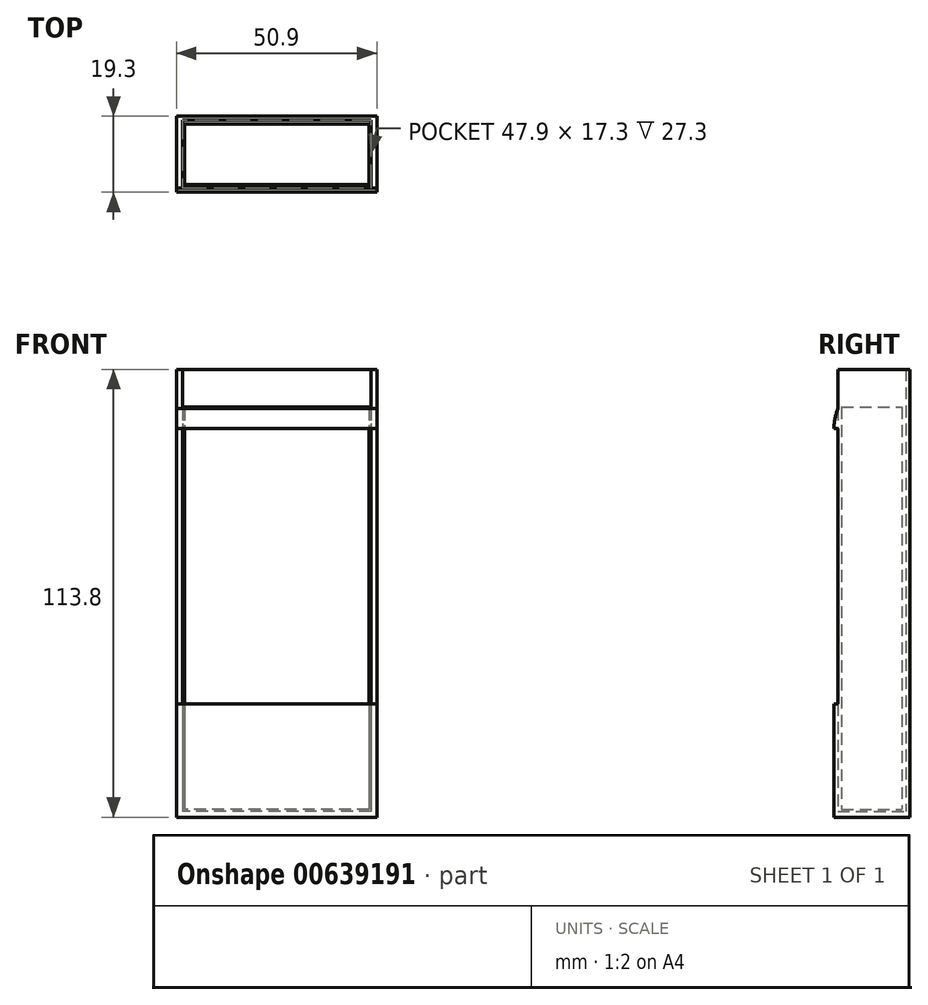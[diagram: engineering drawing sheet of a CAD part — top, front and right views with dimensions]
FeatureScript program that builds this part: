
annotation { "Feature Type Name" : "Feature", "Feature Type Description" : "" }
export const myFeature = defineFeature(function(context is Context, id is Id, definition is map)
    precondition{}
    {
        {
            var Q0;
            Q0=qCreatedBy(makeId("Front.planeOp"),FACE);
            var sketch = newSketch(context, id + "F0", { "sketchPlane" : qUnion([Q0])});
            skLineSegment(sketch, "E0.bottom", {"start": v(23.45, 54.9) * mm, "end": v(-23.45, 54.9) * mm});
            skLineSegment(sketch, "E0.top", {"start": v(23.45, -54.9) * mm, "end": v(-23.45, -54.9) * mm});
            skLineSegment(sketch, "E0.left", {"start": v(23.45, 54.9) * mm, "end": v(23.45, -54.9) * mm});
            skLineSegment(sketch, "E0.right", {"start": v(-23.45, 54.9) * mm, "end": v(-23.45, -54.9) * mm});
            skPoint(sketch, "E0.middle", {"position": v(0, 0) * mm});
            skSolve(sketch);
        }
        {
            var Q0;
            Q0=makeQuery(id+"F0.imprint","IMPRINT",FACE,{"disambiguationData":[TD([[makeQuery(id+"F0.imprint","IMPRINT",EDGE,{"derivedFrom":sQuery(id+"F0.wireOp",EDGE,"E0.bottom")}),1.0]])]});
            extrude(context, id + "F1", {"entities" : qUnion([Q0]), "depth" : 15.3 * mm, "offsetDistance" : 25 * mm});
        }
        {
            var Q0;
            Q0=qCreatedBy(makeId("Front.planeOp"),FACE);
            cPlane(context, id + "F2", {"entities" : qUnion([Q0]), "cplaneType" : CPlaneType.OFFSET, "offset" : 1 * mm, "oppositeDirection" : true, "width" : 150 * mm, "height" : 150 * mm});
        }
        {
            var Q0;
            Q0=qCreatedBy(id+"F2.planeOp",FACE);
            var sketch = newSketch(context, id + "F3", { "sketchPlane" : qUnion([Q0])});
            skLineSegment(sketch, "E1.bottom", {"start": v(25.45, 56.9) * mm, "end": v(-25.45, 56.9) * mm});
            skLineSegment(sketch, "E1.top", {"start": v(25.45, -56.9) * mm, "end": v(-25.45, -56.9) * mm});
            skLineSegment(sketch, "E1.left", {"start": v(25.45, 56.9) * mm, "end": v(25.45, -56.9) * mm});
            skLineSegment(sketch, "E1.right", {"start": v(-25.45, 56.9) * mm, "end": v(-25.45, -56.9) * mm});
            skPoint(sketch, "E1.middle", {"position": v(0, 0) * mm});
            skSolve(sketch);
        }
        {
            var Q0;
            Q0 = qSketchRegion(id + "F3", true);
            extrude(context, id + "F4", {"entities" : qUnion([Q0]), "oppositeDirection" : true, "depth" : 1 * mm, "offsetDistance" : 25 * mm});
        }
        {
            var Q0;
            Q0=qCreatedBy(id+"F2.planeOp",FACE);
            cPlane(context, id + "F5", {"entities" : qUnion([Q0]), "cplaneType" : CPlaneType.OFFSET, "offset" : 0 * mm, "width" : 150 * mm, "height" : 150 * mm});
        }
        {
            var Q0;
            Q0=qCreatedBy(id+"F5.planeOp",FACE);
            var sketch = newSketch(context, id + "F6", { "sketchPlane" : qUnion([Q0])});
            skLineSegment(sketch, "E2.bottom", {"start": v(23.95, 55.4) * mm, "end": v(-23.95, 55.4) * mm});
            skLineSegment(sketch, "E2.top", {"start": v(23.95, -55.4) * mm, "end": v(-23.95, -55.4) * mm});
            skLineSegment(sketch, "E2.left", {"start": v(23.95, 55.4) * mm, "end": v(23.95, -55.4) * mm});
            skLineSegment(sketch, "E2.right", {"start": v(-23.95, 55.4) * mm, "end": v(-23.95, -55.4) * mm});
            skPoint(sketch, "E2.middle", {"position": v(0, 0) * mm});
            skLineSegment(sketch, "E3.bottom", {"start": v(25.45, -56.9) * mm, "end": v(-25.45, -56.9) * mm});
            skLineSegment(sketch, "E3.top", {"start": v(25.45, 56.9) * mm, "end": v(-25.45, 56.9) * mm});
            skLineSegment(sketch, "E3.left", {"start": v(25.45, -56.9) * mm, "end": v(25.45, 56.9) * mm});
            skLineSegment(sketch, "E3.right", {"start": v(-25.45, -56.9) * mm, "end": v(-25.45, 56.9) * mm});
            skSolve(sketch);
        }
        {
            var Q0;
            Q0=makeQuery(id+"F1.opExtrude","CAP_FACE",FACE,{"disambiguationData":[OSD([sQuery(id+"F0.wireOp",EDGE,"E0.bottom"),sQuery(id+"F0.wireOp",EDGE,"E0.top"),sQuery(id+"F0.wireOp",EDGE,"E0.left"),sQuery(id+"F0.wireOp",EDGE,"E0.right")])],"isStart":false});
            cPlane(context, id + "F7", {"entities" : qUnion([Q0]), "cplaneType" : CPlaneType.OFFSET, "offset" : 1 * mm, "width" : 150 * mm, "height" : 150 * mm});
        }
        {
            var Q0;
            Q0=qCreatedBy(id+"F7.planeOp",FACE);
            var sketch = newSketch(context, id + "F8", { "sketchPlane" : qUnion([Q0])});
            skLineSegment(sketch, "E4.bottom", {"start": v(25.45, 56.9) * mm, "end": v(-25.45, 56.9) * mm});
            skLineSegment(sketch, "E4.top", {"start": v(25.45, -56.9) * mm, "end": v(-25.45, -56.9) * mm});
            skLineSegment(sketch, "E4.left", {"start": v(25.45, 56.9) * mm, "end": v(25.45, -56.9) * mm});
            skLineSegment(sketch, "E4.right", {"start": v(-25.45, 56.9) * mm, "end": v(-25.45, -56.9) * mm});
            skPoint(sketch, "E4.middle", {"position": v(0, 0) * mm});
            skSolve(sketch);
        }
        {
            var Q0;
            Q0 = qSketchRegion(id + "F8", true);
            extrude(context, id + "F9", {"entities" : qUnion([Q0]), "operationType" : NewBodyOperationType.ADD, "depth" : 1 * mm, "offsetDistance" : 25 * mm});
        }
        {
            var Q0;
            Q0 = qSketchRegion(id + "F6", true);
            extrude(context, id + "F10", {"entities" : qUnion([Q0]), "operationType" : NewBodyOperationType.ADD, "endBound" : BoundingType.UP_TO_NEXT, "depth" : 25 * mm, "offsetDistance" : 25 * mm});
        }
        {
            var Q0;
            Q0=qCreatedBy(id+"F7.planeOp",FACE);
            cPlane(context, id + "F11", {"entities" : qUnion([Q0]), "cplaneType" : CPlaneType.OFFSET, "offset" : 25 * mm, "width" : 150 * mm, "height" : 150 * mm});
        }
        {
            var Q0;
            Q0=qCreatedBy(id+"F11.planeOp",FACE);
            var sketch = newSketch(context, id + "F12", { "sketchPlane" : qUnion([Q0])});
            skLineSegment(sketch, "E5.bottom", {"start": v(-25.45, 56.9) * mm, "end": v(25.45, 56.9) * mm});
            skLineSegment(sketch, "E5.top", {"start": v(-25.45, -28.1) * mm, "end": v(25.45, -28.1) * mm});
            skLineSegment(sketch, "E5.left", {"start": v(-25.45, 56.9) * mm, "end": v(-25.45, -28.1) * mm});
            skLineSegment(sketch, "E5.right", {"start": v(25.45, 56.9) * mm, "end": v(25.45, -28.1) * mm});
            skSolve(sketch);
        }
        {
            var Q0;
            Q0 = qSketchRegion(id + "F12", true);
            var Q1;
            Q1=qCreatedBy(id+"F7.planeOp",FACE);
            extrude(context, id + "F13", {"entities" : qUnion([Q0]), "operationType" : NewBodyOperationType.REMOVE, "endBound" : BoundingType.UP_TO_SURFACE, "oppositeDirection" : true, "depth" : 25 * mm, "endBoundEntityFace" : qUnion([Q1]), "offsetDistance" : 25 * mm});
        }
        {
            var Q0;
            Q0=qCreatedBy(id+"F7.planeOp",FACE);
            var sketch = newSketch(context, id + "F14", { "sketchPlane" : qUnion([Q0])});
            skLineSegment(sketch, "E6.bottom", {"start": v(-23.95, 58.04) * mm, "end": v(23.95, 58.04) * mm});
            skLineSegment(sketch, "E6.top", {"start": v(-23.95, 47.31) * mm, "end": v(23.95, 47.31) * mm});
            skLineSegment(sketch, "E6.left", {"start": v(-23.95, 58.04) * mm, "end": v(-23.95, 47.31) * mm});
            skLineSegment(sketch, "E6.right", {"start": v(23.95, 58.04) * mm, "end": v(23.95, 47.31) * mm});
            skSolve(sketch);
        }
        {
            var Q0;
            Q0 = qSketchRegion(id + "F14", true);
            var Q1;
            Q1=qCreatedBy(id+"F2.planeOp",FACE);
            extrude(context, id + "F15", {"entities" : qUnion([Q0]), "operationType" : NewBodyOperationType.REMOVE, "endBound" : BoundingType.UP_TO_SURFACE, "oppositeDirection" : true, "depth" : 25 * mm, "endBoundEntityFace" : qUnion([Q1]), "offsetDistance" : 25 * mm});
        }
        {
            var Q0;
            Q0=qCreatedBy(id+"F7.planeOp",FACE);
            var sketch = newSketch(context, id + "F16", { "sketchPlane" : qUnion([Q0])});
            skLineSegment(sketch, "E7.bottom", {"start": v(-25.45, 46.9) * mm, "end": v(25.45, 46.9) * mm});
            skLineSegment(sketch, "E7.top", {"start": v(-25.45, 41.9) * mm, "end": v(25.45, 41.9) * mm});
            skLineSegment(sketch, "E7.left", {"start": v(-25.45, 46.9) * mm, "end": v(-25.45, 41.9) * mm});
            skLineSegment(sketch, "E7.right", {"start": v(25.45, 46.9) * mm, "end": v(25.45, 41.9) * mm});
            skSolve(sketch);
        }
        {
            var Q0;
            Q0 = qSketchRegion(id + "F16", true);
            extrude(context, id + "F17", {"entities" : qUnion([Q0]), "operationType" : NewBodyOperationType.ADD, "depth" : 1 * mm, "offsetDistance" : 25 * mm});
        }
        {
            var Q0;
            {var subQ0=sQuery(id+"F12.wireOp",EDGE,"E5.bottom");Q0=makeQuery(id+"F15.boolean.opBoolean","SPLIT",EDGE,{"disambiguationData":[TD([makeQuery(id+"F4.opExtrude","SWEPT_FACE",FACE,{"disambiguationData":[OSD([sQuery(id+"F3.wireOp",EDGE,"E1.left")])]})])],"derivedFrom":makeQuery(id+"F13.boolean.opBoolean","COPY",EDGE,{"derivedFrom":makeQuery(id+"F13.opExtrude","CAP_EDGE",EDGE,{"disambiguationData":[OSD([subQ0])],"isStart":false})})});}
            var Q1;
            {var subQ0=sQuery(id+"F12.wireOp",EDGE,"E5.bottom");Q1=makeQuery(id+"F15.boolean.opBoolean","SPLIT",EDGE,{"disambiguationData":[TD([makeQuery(id+"F4.opExtrude","SWEPT_FACE",FACE,{"disambiguationData":[OSD([sQuery(id+"F3.wireOp",EDGE,"E1.right")])]})])],"derivedFrom":makeQuery(id+"F13.boolean.opBoolean","COPY",EDGE,{"derivedFrom":makeQuery(id+"F13.opExtrude","CAP_EDGE",EDGE,{"disambiguationData":[OSD([subQ0])],"isStart":false})})});}
            var Q2;
            Q2=makeQuery(id+"F17.opExtrude","CAP_EDGE",EDGE,{"disambiguationData":[OSD([sQuery(id+"F16.wireOp",EDGE,"E7.bottom")])],"isStart":false});
            fillet(context, id + "F18", {"entities" : qUnion([Q0, Q1, Q2]), "radius" : 18.83 * mm, "tangentPropagation" : true, "allowEdgeOverflow" : false});
        }
    });
